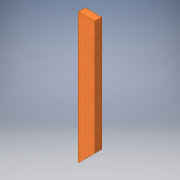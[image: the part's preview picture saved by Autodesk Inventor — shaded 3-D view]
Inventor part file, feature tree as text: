
AUTODESK INVENTOR PART (.ipt)
format: ipt  version: 2016 (Build 200138000, 138)  size: 98,816 bytes
history: native  units: in
note: dims shown in document units (in); Inventor stores cm internally (conversion verified against a paired STEP export)
features: extrude x1, sketch x1
ambient origin geometry x8: Origin, YZ Plane, XZ Plane, XY Plane, X Axis, Y Axis, Z Axis, Center Point
bodies: Body1 (feature_tree)
feature tree (2):
  extrude  "Extrusion2"  Depth=1.5in
  sketch  "Sketch3"  dims[d16=45.0deg d17=27.864in d18=3.5in d19=1.5in d20=0.0in]
